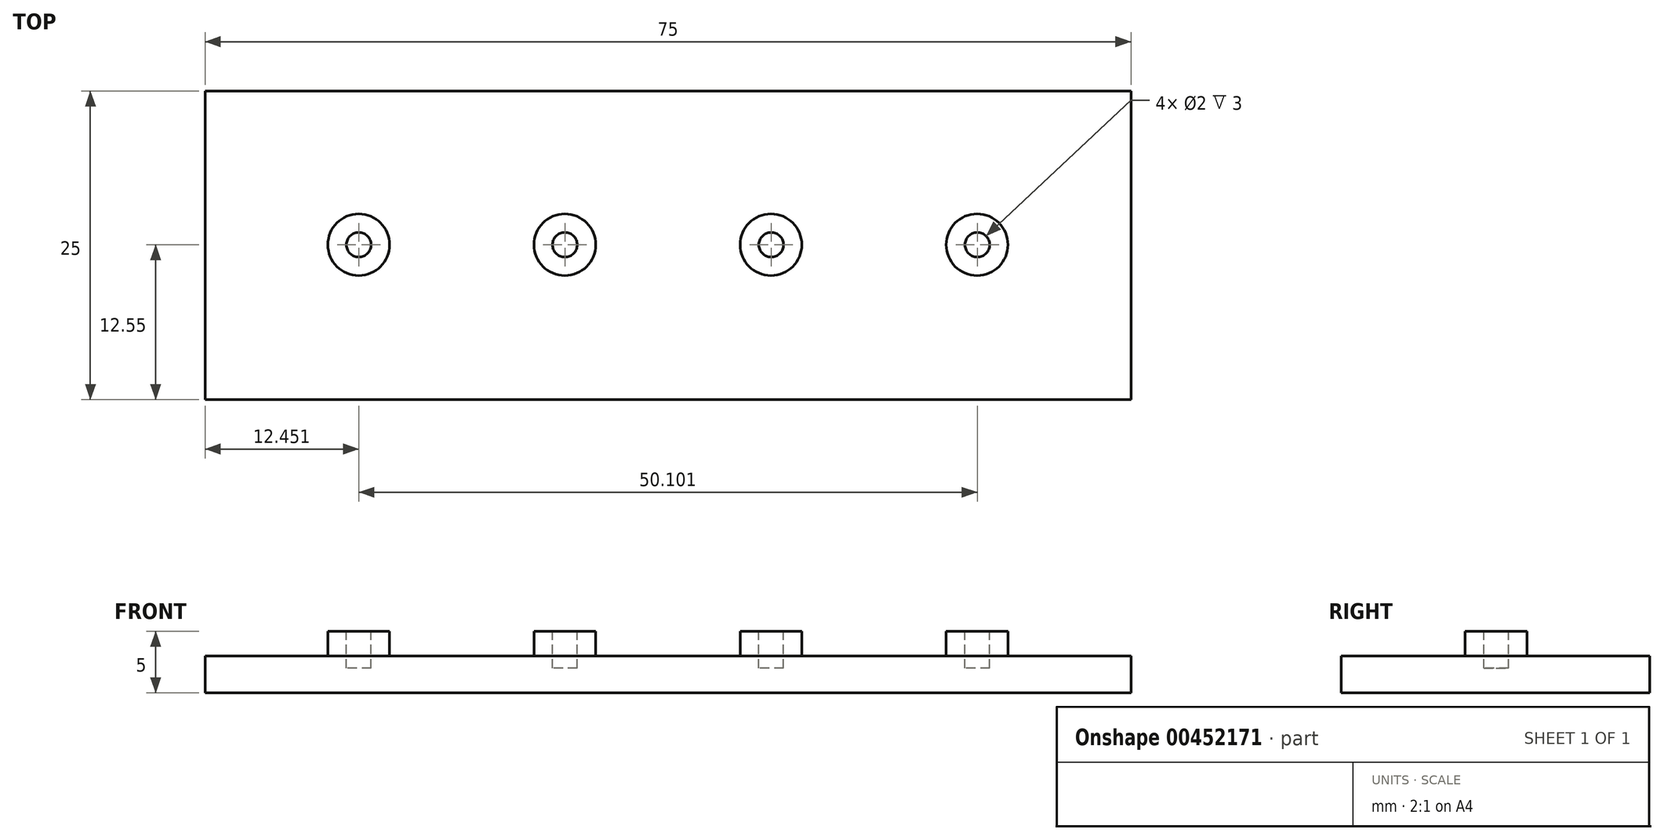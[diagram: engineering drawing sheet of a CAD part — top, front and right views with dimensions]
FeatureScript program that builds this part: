
annotation { "Feature Type Name" : "Feature", "Feature Type Description" : "" }
export const myFeature = defineFeature(function(context is Context, id is Id, definition is map)
    precondition{}
    {
        {
            var Q0;
            Q0=qCreatedBy(makeId("Top.planeOp"),FACE);
            var sketch = newSketch(context, id + "F0", { "sketchPlane" : qUnion([Q0])});
            skLineSegment(sketch, "E0.bottom", {"start": v(-37.45, 12.45) * mm, "end": v(37.55, 12.45) * mm});
            skLineSegment(sketch, "E0.top", {"start": v(-37.45, -12.55) * mm, "end": v(37.55, -12.55) * mm});
            skLineSegment(sketch, "E0.left", {"start": v(-37.45, 12.45) * mm, "end": v(-37.45, -12.55) * mm});
            skLineSegment(sketch, "E0.right", {"start": v(37.55, 12.45) * mm, "end": v(37.55, -12.55) * mm});
            skLineSegment(sketch, "E1", {"start": v(-37.45, -0.05) * mm, "end": v(37.55, -0.05) * mm, "construction": true});
            skLineSegment(sketch, "E2", {"start": v(0, 12.45) * mm, "end": v(0, -12.55) * mm, "construction": true});
            skLineSegment(sketch, "E3", {"start": v(-25, 12.45) * mm, "end": v(-25, -12.47) * mm, "construction": true});
            skCircle(sketch, "E4", {"center": v(-25, 0) * mm, "radius": 5 * mm, "construction": true});
            skCircle(sketch, "E5.1.0.0", {"center": v(-8.3, 0) * mm, "radius": 5 * mm, "construction": true});
            skCircle(sketch, "E5.2.0.0", {"center": v(8.4, 0) * mm, "radius": 5 * mm, "construction": true});
            skCircle(sketch, "E5.3.0.0", {"center": v(25.1, 0) * mm, "radius": 5 * mm, "construction": true});
            skLineSegment(sketch, "E5.direction1", {"start": v(-25, 0) * mm, "end": v(-8.3, 0) * mm, "construction": true});
            skLineSegment(sketch, "E6", {"start": v(25.1, -12.55) * mm, "end": v(25.1, 12.45) * mm, "construction": true});
            skSolve(sketch);
        }
        {
            var Q0;
            Q0 = qSketchRegion(id + "F0", true);
            extrude(context, id + "F1", {"entities" : qUnion([Q0]), "depth" : 3 * mm});
        }
        {
            var Q0;
            Q0=qCreatedBy(makeId("Top.planeOp"),FACE);
            var sketch = newSketch(context, id + "F2", { "sketchPlane" : qUnion([Q0])});
            skCircle(sketch, "E7", {"center": v(-25, 0) * mm, "radius": 2.5 * mm});
            skCircle(sketch, "E8", {"center": v(-8.3, 0) * mm, "radius": 2.5 * mm});
            skCircle(sketch, "E9", {"center": v(8.39, 0) * mm, "radius": 2.5 * mm});
            skCircle(sketch, "E10", {"center": v(25.08, 0) * mm, "radius": 2.5 * mm});
            skSolve(sketch);
        }
        {
            var Q0;
            Q0 = qSketchRegion(id + "F2", true);
            extrude(context, id + "F3", {"entities" : qUnion([Q0]), "operationType" : NewBodyOperationType.ADD, "depth" : 5 * mm});
        }
        {
            var Q0;
            Q0=makeQuery(id+"F3.opExtrude","CAP_FACE",FACE,{"disambiguationData":[OSD([sQuery(id+"F2.wireOp",EDGE,"E7")])],"isStart":false});
            var sketch = newSketch(context, id + "F4", { "sketchPlane" : qUnion([Q0])});
            skCircle(sketch, "E11", {"center": v(-25, 0) * mm, "radius": 1 * mm});
            skCircle(sketch, "E12", {"center": v(-8.3, 0) * mm, "radius": 1 * mm});
            skCircle(sketch, "E13", {"center": v(8.4, 0) * mm, "radius": 1 * mm});
            skCircle(sketch, "E14", {"center": v(25.1, 0) * mm, "radius": 1 * mm});
            skSolve(sketch);
        }
        {
            var Q0;
            Q0=makeQuery(id+"F4.imprint","IMPRINT",FACE,{"disambiguationData":[TD([[makeQuery(id+"F4.imprint","IMPRINT",EDGE,{"derivedFrom":sQuery(id+"F4.wireOp",EDGE,"E11")}),1.0]])]});
            var Q1;
            Q1=makeQuery(id+"F4.imprint","IMPRINT",FACE,{"disambiguationData":[TD([[makeQuery(id+"F4.imprint","IMPRINT",EDGE,{"derivedFrom":sQuery(id+"F4.wireOp",EDGE,"E12")}),1.0]])]});
            var Q2;
            Q2=makeQuery(id+"F4.imprint","IMPRINT",FACE,{"disambiguationData":[TD([[makeQuery(id+"F4.imprint","IMPRINT",EDGE,{"derivedFrom":sQuery(id+"F4.wireOp",EDGE,"E13")}),1.0]])]});
            var Q3;
            Q3=makeQuery(id+"F4.imprint","IMPRINT",FACE,{"disambiguationData":[TD([[makeQuery(id+"F4.imprint","IMPRINT",EDGE,{"derivedFrom":sQuery(id+"F4.wireOp",EDGE,"E14")}),1.0]])]});
            var Q4;
            Q4=sQuery(id+"F4.wireOp",EDGE,"E11");
            var Q5;
            Q5=sQuery(id+"F4.wireOp",EDGE,"E12");
            var Q6;
            Q6=sQuery(id+"F4.wireOp",EDGE,"E13");
            var Q7;
            Q7=sQuery(id+"F4.wireOp",EDGE,"E14");
            extrude(context, id + "F5", {"entities" : qUnion([Q0, Q1, Q2, Q3]), "operationType" : NewBodyOperationType.REMOVE, "surfaceEntities" : qUnion([Q4, Q5, Q6, Q7]), "oppositeDirection" : true, "depth" : 3 * mm});
        }
    });
